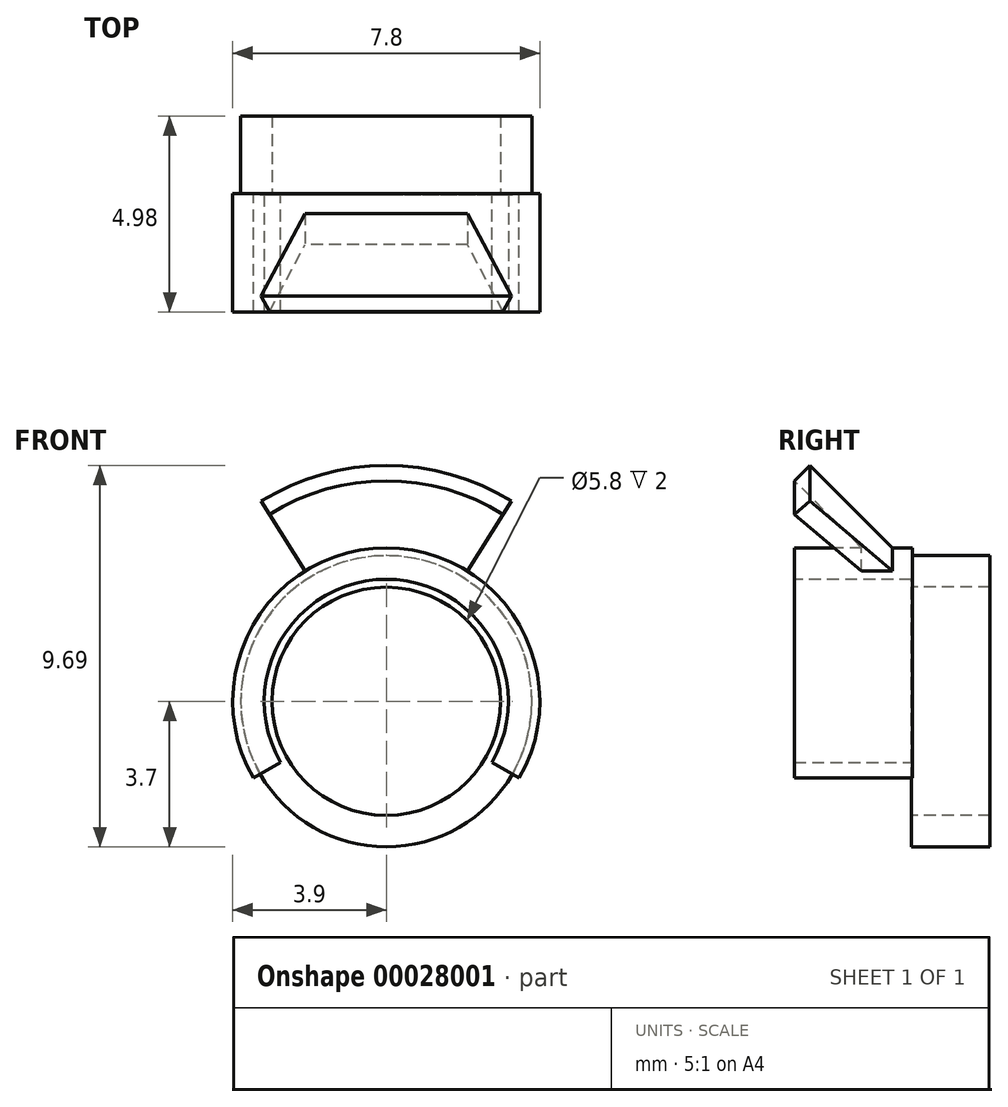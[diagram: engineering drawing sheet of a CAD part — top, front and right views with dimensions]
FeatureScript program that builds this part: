
annotation { "Feature Type Name" : "Feature", "Feature Type Description" : "" }
export const myFeature = defineFeature(function(context is Context, id is Id, definition is map)
    precondition{}
    {
        {
            var Q0;
            Q0=qCreatedBy(makeId("Right.planeOp"),FACE);
            var sketch = newSketch(context, id + "F0", { "sketchPlane" : qUnion([Q0])});
            skLineSegment(sketch, "E0.bottom", {"start": v(-0.98, 3.9) * mm, "end": v(2.02, 3.9) * mm});
            skLineSegment(sketch, "E0.top", {"start": v(-0.98, 3.1) * mm, "end": v(2.02, 3.1) * mm});
            skLineSegment(sketch, "E0.left", {"start": v(-0.98, 3.9) * mm, "end": v(-0.98, 3.1) * mm});
            skLineSegment(sketch, "E0.right", {"start": v(2.02, 3.9) * mm, "end": v(2.02, 3.1) * mm});
            skLineSegment(sketch, "E1.bottom", {"start": v(-0.98, 3.1) * mm, "end": v(0.22, 3.1) * mm});
            skLineSegment(sketch, "E1.top", {"start": v(-0.98, 2.3) * mm, "end": v(0.22, 2.3) * mm});
            skLineSegment(sketch, "E1.left", {"start": v(-0.98, 3.1) * mm, "end": v(-0.98, 2.3) * mm});
            skLineSegment(sketch, "E1.right", {"start": v(0.22, 3.1) * mm, "end": v(0.22, 2.3) * mm});
            skLineSegment(sketch, "E2", {"start": v(0.22, 3.1) * mm, "end": v(2.02, 3.1) * mm});
            skLineSegment(sketch, "E3", {"start": v(-0.38, 2.3) * mm, "end": v(-0.38, 0) * mm});
            skLineSegment(sketch, "E4", {"start": v(-8.7, 0) * mm, "end": v(0, 0) * mm});
            skLineSegment(sketch, "E5", {"start": v(-0.98, 3.1) * mm, "end": v(-0.98, 3.9) * mm});
            skLineSegment(sketch, "E6", {"start": v(-9.9, 0) * mm, "end": v(-3.58, 0) * mm});
            skSolve(sketch);
        }
        {
            var Q0;
            Q0=makeQuery(id+"F0.imprint","IMPRINT",FACE,{"disambiguationData":[TD([[makeQuery(id+"F0.imprint","IMPRINT",EDGE,{"derivedFrom":sQuery(id+"F0.wireOp",EDGE,"E1.bottom")}),-1.0]])]});
            var Q1;
            Q1=makeQuery(id+"F0.imprint","IMPRINT",FACE,{"disambiguationData":[TD([[makeQuery(id+"F0.imprint","IMPRINT",EDGE,{"derivedFrom":sQuery(id+"F0.wireOp",EDGE,"E0.bottom")}),-1.0]])]});
            var Q2;
            Q2=sQuery(id+"F0.wireOp",EDGE,"E4");
            revolve(context, id + "F1", {"entities" : qUnion([Q0, Q1]), "axis" : qUnion([Q2]), "revolveType" : RevolveType.TWO_DIRECTIONS, "angle" : 120 * degree, "angleBack" : 240 * degree});
        }
        {
            var Q0;
            Q0=qCreatedBy(makeId("Right.planeOp"),FACE);
            var sketch = newSketch(context, id + "F2", { "sketchPlane" : qUnion([Q0])});
            skLineSegment(sketch, "E7", {"start": v(1.55, 3.87) * mm, "end": v(-0.57, 6) * mm});
            skLineSegment(sketch, "E8", {"start": v(-0.57, 6) * mm, "end": v(-0.97, 5.6) * mm});
            skLineSegment(sketch, "E9", {"start": v(-0.97, 5.6) * mm, "end": v(1.56, 3.07) * mm});
            skLineSegment(sketch, "E10", {"start": v(1.56, 3.07) * mm, "end": v(1.55, 3.87) * mm});
            skLineSegment(sketch, "E11", {"start": v(0, 3.87) * mm, "end": v(1.55, 3.87) * mm});
            skLineSegment(sketch, "E12", {"start": v(-6.62, 0) * mm, "end": v(0, 0) * mm});
            skLineSegment(sketch, "E13", {"start": v(-0.97, 5.6) * mm, "end": v(-0.97, 0) * mm});
            skSolve(sketch);
        }
        {
            var Q0;
            Q0=makeQuery(id+"F2.imprint","IMPRINT",FACE,{"disambiguationData":[TD([[makeQuery(id+"F2.imprint","IMPRINT",EDGE,{"derivedFrom":sQuery(id+"F2.wireOp",EDGE,"E7")}),1.0]])]});
            var Q1;
            Q1=sQuery(id+"F2.wireOp",EDGE,"E12");
            revolve(context, id + "F3", {"operationType" : NewBodyOperationType.ADD, "entities" : qUnion([Q0]), "axis" : qUnion([Q1]), "revolveType" : RevolveType.TWO_DIRECTIONS, "angle" : 32 * degree, "angleBack" : 328 * degree});
        }
        {
            var Q0;
            Q0=qCreatedBy(makeId("Right.planeOp"),FACE);
            var sketch = newSketch(context, id + "F4", { "sketchPlane" : qUnion([Q0])});
            skLineSegment(sketch, "E14.bottom", {"start": v(2, 3.7) * mm, "end": v(4, 3.7) * mm});
            skLineSegment(sketch, "E14.top", {"start": v(2, 2.9) * mm, "end": v(4, 2.9) * mm});
            skLineSegment(sketch, "E14.left", {"start": v(2, 3.7) * mm, "end": v(2, 2.9) * mm});
            skLineSegment(sketch, "E14.right", {"start": v(4, 3.7) * mm, "end": v(4, 2.9) * mm});
            skLineSegment(sketch, "E15", {"start": v(0, 0) * mm, "end": v(3.41, 0) * mm});
            skLineSegment(sketch, "E16", {"start": v(0, 3.62) * mm, "end": v(2, 3.62) * mm});
            skLineSegment(sketch, "E17", {"start": v(2.4, 2.9) * mm, "end": v(2.4, 0) * mm});
            skSolve(sketch);
        }
        {
            var Q0;
            Q0=makeQuery(id+"F4.imprint","IMPRINT",FACE,{"disambiguationData":[TD([[makeQuery(id+"F4.imprint","IMPRINT",EDGE,{"derivedFrom":sQuery(id+"F4.wireOp",EDGE,"E14.bottom")}),-1.0]])]});
            var Q1;
            Q1=sQuery(id+"F4.wireOp",EDGE,"E15");
            revolve(context, id + "F5", {"operationType" : NewBodyOperationType.ADD, "entities" : qUnion([Q0]), "axis" : qUnion([Q1]), "revolveType" : RevolveType.FULL});
        }
    });
